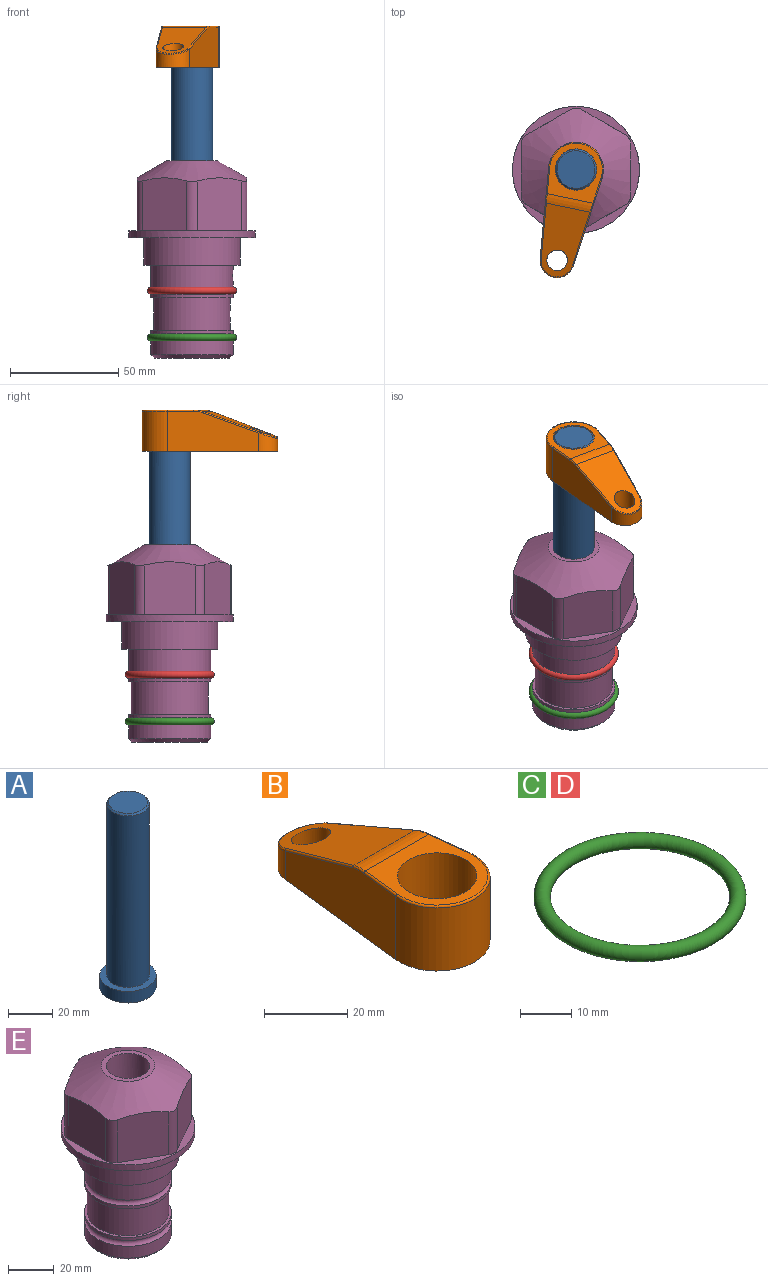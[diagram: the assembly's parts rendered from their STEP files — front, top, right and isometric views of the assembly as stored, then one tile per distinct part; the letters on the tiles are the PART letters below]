
ASSEMBLY  parts=5 mates=3
PART A: 6 faces, bbox 25.4x25.4x101.6 mm
  f0: plane 17.46x17.46mm, normal (0,0,1), area 239.5mm2, adj f5
  f1: plane 25.4x25.4mm, normal (0,0,-1), area 506.7mm2, adj f2
  f2: cylinder r=12.7mm len=25.4mm, axis (0,0,1), area 506.7mm2, adj f1,f3
  f3: plane 25.4x25.4mm, normal (0,0,1), area 221.7mm2, adj f2,f4
  f4: cylinder r=9.53mm len=94.46mm, axis (0,0,1), area 5653mm2, adj f3,f5
  f5: cone r=8.73mm half-angle=45deg, axis (0,0,-1), area 64.4mm2, adj f0,f4
PART B: 44 faces, bbox 27.5x64.5x19.1 mm
  f0: plane 2.3x0.95mm, normal (0,0,-1), area 1mm2, adj f25,f30,f34
  f1: plane 63.5x25.4mm, normal (0,0,-1), area 561.7mm2, adj f2,f3,f4,f5,f6,f7,f19,f20
  f2: cylinder r=12.7mm len=25.4mm, axis (0,0,-1), area 792.2mm2, adj f1,f3,f5,f13
  f3: plane 42.33x18.54mm, normal (0.99,0.11,0), area 647mm2, adj f1,f2,f4,f11,f12,f14
  f4: cylinder r=7.94mm len=15.78mm, axis (0,0,-1), area 158.6mm2, adj f1,f3,f5,f16
  f5: plane 42.33x18.54mm, normal (-0.99,0.11,0), area 647mm2, adj f1,f2,f4,f15,f17,f18
  f6: cylinder r=9.53mm len=19.05mm, axis (0,0,-1), area 1140.1mm2, adj f1,f8
  f7: cylinder r=4.76mm len=10.98mm, axis (0,0,-1), area 276.1mm2, adj f1,f9
  f8: plane 25.83x24.38mm, normal (0,0,1), area 262.2mm2, adj f6,f10,f11,f13,f15
  f9: plane 32.49x20.55mm, normal (0,0.34,0.94), area 489.9mm2, adj f7,f10,f14,f16,f18
  f10: cylinder r=12.7mm len=21.49mm, axis (-1,0,0), area 93.2mm2, adj f8,f9,f12,f17
  f11: cylinder r=0.51mm len=12.34mm, axis (0.11,-0.99,0), area 9.9mm2, adj f3,f8,f12,f13
  f12: bspline ~7.62x1.64mm, area 3.5mm2, adj f3,f10,f11,f14
  f13: torus R=12.19mm, axis (0,0,1), area 33.6mm2, adj f2,f8,f11,f15
  f14: cylinder r=0.51mm len=26.01mm, axis (0.1,-0.93,0.34), area 21.6mm2, adj f3,f9,f12,f16
  f15: cylinder r=0.51mm len=12.34mm, axis (0.11,0.99,0), area 9.9mm2, adj f5,f8,f13,f17
  f16: bspline ~15.78x7.05mm, area 15.7mm2, adj f4,f9,f14,f18
  f17: bspline ~7.62x1.64mm, area 3.5mm2, adj f5,f10,f15,f18
  f18: cylinder r=0.51mm len=26.01mm, axis (0.1,0.93,-0.34), area 21.6mm2, adj f5,f9,f16,f17
  f19: plane 21.6x14.29mm, normal (-0.99,-0.11,0), area 242.6mm2, adj f1,f26,f28,f34,f36,f38
  f20: plane 21.6x14.29mm, normal (0.99,-0.11,0), area 242.6mm2, adj f1,f27,f29,f37,f39,f41
  f21: cylinder r=12.7mm len=14.29mm, axis (0,0,-1), area 173.2mm2, adj f1,f26,f27,f30,f31,f33
  f22: cylinder r=7.94mm len=7.63mm, axis (0,0,-1), area 53.8mm2, adj f1,f28,f29,f42
  f23: plane 2.3x0.95mm, normal (0,0,-1), area 1mm2, adj f25,f33,f37
  f24: plane 17.94x12.32mm, normal (0,-0.34,-0.94), area 191.2mm2, adj f25,f38,f41,f42
  f25: cylinder r=9.53mm len=12.93mm, axis (-1,0,0), area 37.5mm2, adj f0,f23,f24,f31,f36,f39
  f26: cylinder r=1.59mm len=14.29mm, axis (0,0,-1), area 49mm2, adj f1,f19,f21,f32
  f27: cylinder r=1.59mm len=14.29mm, axis (0,0,-1), area 49mm2, adj f1,f20,f21,f35
  f28: cylinder r=1.59mm len=7.28mm, axis (0,0,-1), area 22.1mm2, adj f1,f19,f22,f40
  f29: cylinder r=1.59mm len=7.28mm, axis (0,0,-1), area 22.1mm2, adj f1,f20,f22,f43
  f30: torus R=14.29mm, axis (0,0,1), area 5.8mm2, adj f0,f21,f31,f32
  f31: bspline ~11.06x2.73mm, area 20.8mm2, adj f21,f25,f30,f33
  f32: sphere r=1.59mm, area 5.4mm2, adj f26,f30,f34
  f33: torus R=14.29mm, axis (0,0,1), area 5.8mm2, adj f21,f23,f31,f35
  f34: cylinder r=1.59mm len=1.68mm, axis (-0.11,0.99,0), area 2.4mm2, adj f0,f19,f32,f36
  f35: sphere r=1.59mm, area 5.4mm2, adj f27,f33,f37
  f36: bspline ~5.82x2.33mm, area 7.7mm2, adj f19,f25,f34,f38
  f37: cylinder r=1.59mm len=1.68mm, axis (0.11,0.99,0), area 2.4mm2, adj f20,f23,f35,f39
  f38: cylinder r=1.59mm len=18.33mm, axis (0.1,-0.93,0.34), area 46.7mm2, adj f19,f24,f36,f40
  f39: bspline ~5.82x2.33mm, area 7.7mm2, adj f20,f25,f37,f41
  f40: sphere r=1.59mm, area 3.6mm2, adj f28,f38,f42
  f41: cylinder r=1.59mm len=18.33mm, axis (0.1,0.93,-0.34), area 46.7mm2, adj f20,f24,f39,f43
  f42: bspline ~8.31x1.84mm, area 15.3mm2, adj f22,f24,f40,f43
  f43: sphere r=1.59mm, area 3.6mm2, adj f29,f41,f42
PART C: 1 faces, bbox 44.7x44.7x3.2 mm
  f0: torus R=19.05mm, axis (0,0,1), area 1193.9mm2
PART D: same geometry as C
PART E: 36 faces, bbox 58.7x58.7x91.2 mm
  f0: cylinder r=17.78mm len=35.56mm, axis (0,0,1), area 1670.8mm2, adj f23,f24,f31
  f1: cylinder r=19.05mm len=38.1mm, axis (0,0,1), area 1191.9mm2, adj f26,f27,f30
  f2: plane 58.66x58.66mm, normal (0,0,-1), area 1150.6mm2, adj f3,f28
  f3: cylinder r=29.33mm len=58.66mm, axis (0,0,-1), area 585.1mm2, adj f2,f4
  f4: plane 58.66x58.66mm, normal (0,0,1), area 475.9mm2, adj f3,f5,f6,f7,f8,f9,f10,f11
  f5: plane 24.5x20.32mm, normal (-0.5,0.87,0), area 562.8mm2, adj f4,f15,f16,f17
  f6: plane 24.5x20.32mm, normal (0.5,0.87,0), area 562.8mm2, adj f4,f14,f15,f17
  f7: plane 24.5x23.48mm, normal (1,0,0), area 562.8mm2, adj f4,f13,f14,f17
  f8: plane 24.5x20.32mm, normal (0.5,-0.87,0), area 562.8mm2, adj f4,f12,f13,f17
  f9: plane 24.5x20.32mm, normal (-0.5,-0.87,0), area 562.8mm2, adj f4,f11,f12,f17
  f10: plane 24.5x23.48mm, normal (-1,0,0), area 562.8mm2, adj f4,f11,f16,f17
  f11: cylinder r=5.08mm len=23.01mm, axis (0,0,-1), area 121.2mm2, adj f4,f9,f10,f17
  f12: cylinder r=5.08mm len=23.01mm, axis (0,0,-1), area 121.2mm2, adj f4,f8,f9,f17
  f13: cylinder r=5.08mm len=23.01mm, axis (0,0,-1), area 121.2mm2, adj f4,f7,f8,f17
  f14: cylinder r=5.08mm len=23.01mm, axis (0,0,-1), area 121.2mm2, adj f4,f6,f7,f17
  f15: cylinder r=5.08mm len=23.01mm, axis (0,0,-1), area 121.2mm2, adj f4,f5,f6,f17
  f16: cylinder r=5.08mm len=23.01mm, axis (0,0,-1), area 121.2mm2, adj f4,f5,f10,f17
  f17: cone r=11.73mm half-angle=60deg, axis (0,0,-1), area 2071.8mm2, adj f5,f6,f7,f8,f9,f10,f11,f12
  f18: plane 23.46x23.46mm, normal (0,0,1), area 147.4mm2, adj f17,f35
  f19: plane 34.93x34.93mm, normal (0,0,-1), area 958mm2, adj f29
  f20: cylinder r=19.05mm len=38.1mm, axis (0,0,1), area 760.1mm2, adj f21,f29
  f21: torus R=19.05mm, axis (0,0,1), area 565.3mm2, adj f20,f22
  f22: cylinder r=19.05mm len=38.1mm, axis (0,0,1), area 190mm2, adj f21,f23
  f23: plane 38.1x38.1mm, normal (0,0,1), area 146.9mm2, adj f0,f22
  f24: plane 38.1x38.1mm, normal (0,0,-1), area 146.9mm2, adj f0,f25
  f25: cylinder r=19.05mm len=38.1mm, axis (0,0,1), area 190mm2, adj f24,f26
  f26: torus R=19.05mm, axis (0,0,1), area 565.3mm2, adj f1,f25
  f27: plane 44.45x44.45mm, normal (0,0,-1), area 411.7mm2, adj f1,f28
  f28: cylinder r=22.23mm len=44.45mm, axis (0,0,1), area 1773.5mm2, adj f2,f27
  f29: cone r=19.05mm half-angle=45deg, axis (0,0,1), area 257.5mm2, adj f19,f20
  f30: cylinder r=3.17mm len=6.75mm, axis (-1,0,0), area 128mm2, adj f1,f33
  f31: cylinder r=3.17mm len=6.35mm, axis (-1,0,0), area 102.5mm2, adj f0,f33
  f32: plane 25.4x25.4mm, normal (0,0,1), area 506.7mm2, adj f33
  f33: cylinder r=12.7mm len=66.42mm, axis (0,0,-1), area 5236.2mm2, adj f30,f31,f32,f34
  f34: cone r=9.53mm half-angle=30deg, axis (0,0,-1), area 443.4mm2, adj f33,f35
  f35: cylinder r=9.53mm len=19.05mm, axis (0,0,-1), area 849mm2, adj f18,f34
PLACE A rot(axis=(0,0,-1),101.7deg) t=(0,0,24.16)mm
PLACE B rot(axis=(0,0,1),168.3deg) t=(0,0,78.77)mm
PLACE C t=(0,0,-21.59)mm
PLACE D at identity
PLACE E at identity fixed
MATE fastened C.f0 <-> E.f0  axis (0,0,1) through (0,0,-46.1)mm
MATE cylindrical A.f2 <-> E.f0  axis (0,0,1) through (0,0,49.79)mm
MATE fastened B.f2 <-> A.f2  axis (0,0,1) through (0,0,97.82)mm
